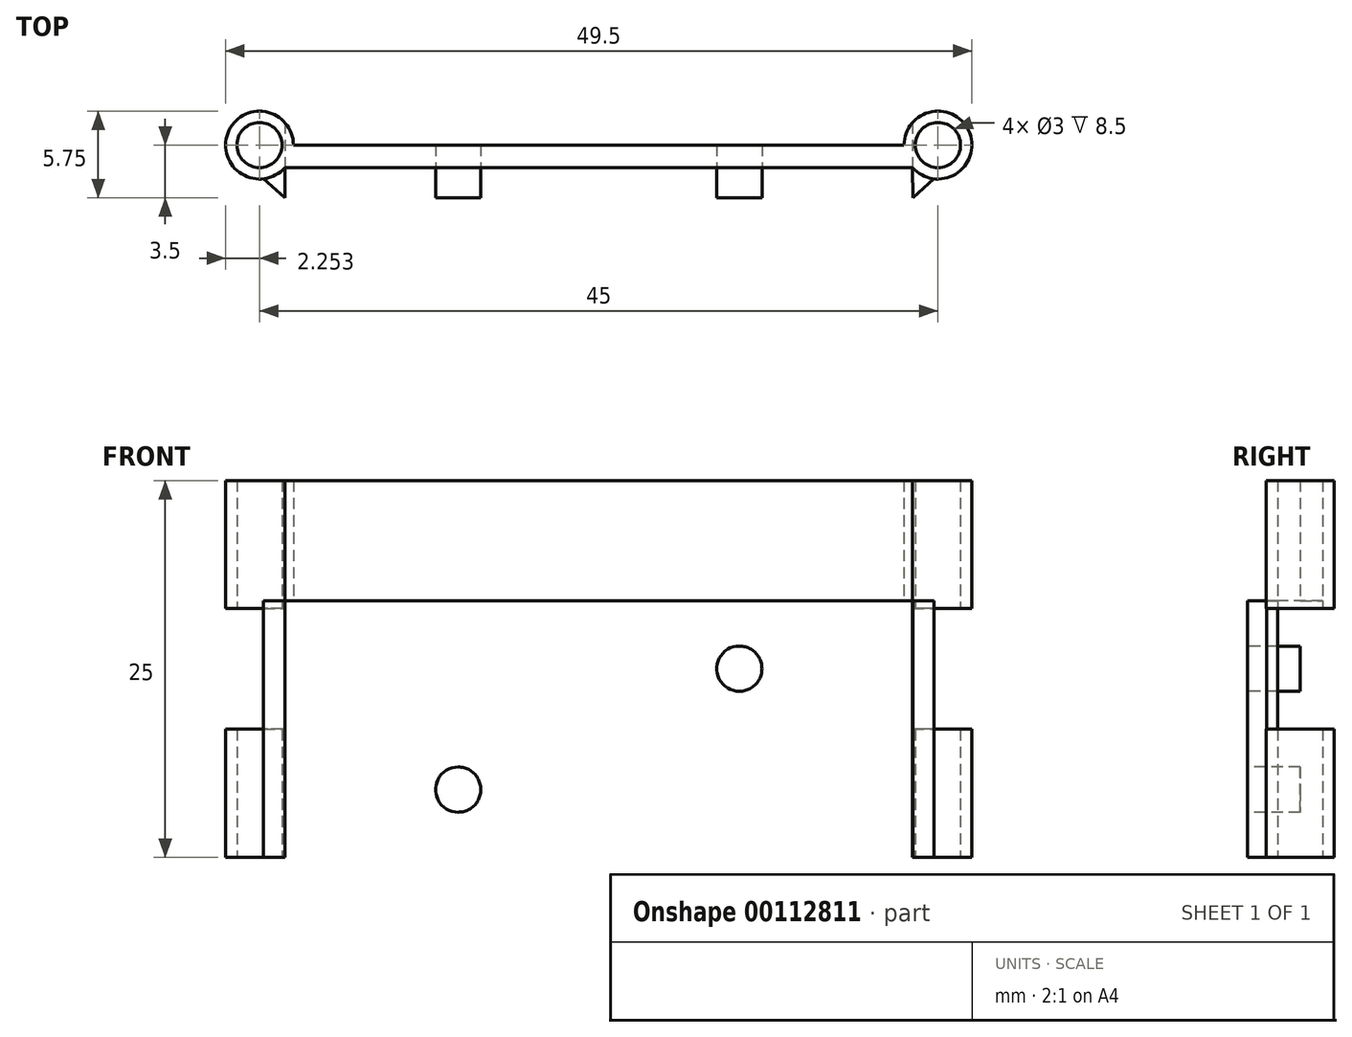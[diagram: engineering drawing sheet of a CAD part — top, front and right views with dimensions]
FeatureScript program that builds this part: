
annotation { "Feature Type Name" : "Feature", "Feature Type Description" : "" }
export const myFeature = defineFeature(function(context is Context, id is Id, definition is map)
    precondition{}
    {
        {
            var Q0;
            Q0=qCreatedBy(makeId("Top.planeOp"),FACE);
            var sketch = newSketch(context, id + "F0", { "sketchPlane" : qUnion([Q0])});
            skCircle(sketch, "E0", {"center": v(24.85, 0) * mm, "radius": 1.5 * mm});
            skCircle(sketch, "E1", {"center": v(-20.15, 0) * mm, "radius": 1.5 * mm});
            skLineSegment(sketch, "E2", {"start": v(-17.9, 0) * mm, "end": v(22.6, 0) * mm});
            skArc(sketch, "E3", {"start": v(-17.9, 0) * mm, "mid": v(-22.25, 0.8) * mm, "end": v(-18.47, -1.5) * mm});
            skArc(sketch, "E4", {"start": v(23.16, -1.49) * mm, "mid": v(26.96, 0.8) * mm, "end": v(22.6, 0) * mm});
            skPoint(sketch, "E5.orphan", {"position": v(-18.65, 0) * mm});
            skLineSegment(sketch, "E6.trimOffspring", {"start": v(23.16, -1.49) * mm, "end": v(-18.47, -1.5) * mm});
            skSolve(sketch);
        }
        {
            var Q0;
            Q0=makeQuery(id+"F0.imprint","IMPRINT",FACE,{"disambiguationData":[TD([[makeQuery(id+"F0.imprint","IMPRINT",EDGE,{"derivedFrom":sQuery(id+"F0.wireOp",EDGE,"E0")}),-1.0]])]});
            extrude(context, id + "F1", {"entities" : qUnion([Q0]), "depth" : 25 * mm});
        }
        {
            var Q0;
            Q0=makeQuery(id+"F1.opExtrude","CAP_FACE",FACE,{"disambiguationData":[OSD([sQuery(id+"F0.wireOp",EDGE,"E0"),sQuery(id+"F0.wireOp",EDGE,"E1"),sQuery(id+"F0.wireOp",EDGE,"E2"),sQuery(id+"F0.wireOp",EDGE,"E3"),sQuery(id+"F0.wireOp",EDGE,"E4"),sQuery(id+"F0.wireOp",EDGE,"E6.trimOffspring")])],"isStart":false});
            cPlane(context, id + "F2", {"entities" : qUnion([Q0]), "cplaneType" : CPlaneType.OFFSET, "offset" : 12.5 * mm, "oppositeDirection" : true, "width" : 152.4 * mm, "height" : 152.4 * mm});
        }
        {
            var Q0;
            Q0=qCreatedBy(id+"F2.planeOp",FACE);
            var sketch = newSketch(context, id + "F3", { "sketchPlane" : qUnion([Q0])});
            skCircle(sketch, "E7", {"center": v(-20.15, 0) * mm, "radius": 2.25 * mm});
            skCircle(sketch, "E8", {"center": v(24.85, 0) * mm, "radius": 2.25 * mm});
            skSolve(sketch);
        }
        {
            var Q0;
            Q0 = qSketchRegion(id + "F3", true);
            extrude(context, id + "F4", {"entities" : qUnion([Q0]), "operationType" : NewBodyOperationType.REMOVE, "oppositeDirection" : true, "depth" : 4 * mm, "hasSecondDirection" : true, "secondDirectionOppositeDirection" : false, "secondDirectionDepth" : 4 * mm});
        }
        {
            var Q0;
            Q0=makeQuery(id+"F1.opExtrude","CAP_FACE",FACE,{"disambiguationData":[OSD([sQuery(id+"F0.wireOp",EDGE,"E0"),sQuery(id+"F0.wireOp",EDGE,"E1"),sQuery(id+"F0.wireOp",EDGE,"E2"),sQuery(id+"F0.wireOp",EDGE,"E3"),sQuery(id+"F0.wireOp",EDGE,"E4"),sQuery(id+"F0.wireOp",EDGE,"E6.trimOffspring")])],"isStart":true});
            var sketch = newSketch(context, id + "F5", { "sketchPlane" : qUnion([Q0])});
            skLineSegment(sketch, "E9.0", {"start": v(23.18, 3.49) * mm, "end": v(-18.47, 3.5) * mm});
            skLineSegment(sketch, "E10", {"start": v(-18.47, 3.5) * mm, "end": v(-19.9, 2.24) * mm});
            skLineSegment(sketch, "E11", {"start": v(2.35, 1.5) * mm, "end": v(2.35, 0) * mm, "construction": true});
            skPoint(sketch, "E11.endSnap0", {"position": v(2.35, 0) * mm});
            skLineSegment(sketch, "E12.MirrorCS", {"start": v(23.18, 3.49) * mm, "end": v(24.6, 2.22) * mm});
            skSolve(sketch);
        }
        {
            var Q0;
            {var subQ3=sQuery(id+"F5.wireOp",EDGE,"E9.0");Q0=makeQuery(id+"F5.imprint","IMPRINT",FACE,{"disambiguationData":[TD([[makeQuery(id+"F5.imprint","IMPRINT",EDGE,{"derivedFrom":subQ3}),1.0]])]});}
            var Q1;
            Q1=makeQuery(id+"F4.boolean.opBoolean","COPY",FACE,{"derivedFrom":makeQuery(id+"F4.opExtrude","CAP_FACE",FACE,{"disambiguationData":[OSD([sQuery(id+"F3.wireOp",EDGE,"E8")])],"isStart":true})});
            extrude(context, id + "F6", {"entities" : qUnion([Q0]), "operationType" : NewBodyOperationType.ADD, "oppositeDirection" : true, "endBoundEntityFace" : qUnion([Q1]), "depth" : 17.02 * mm});
        }
        {
            var Q0;
            Q0=makeQuery(id+"F6.opExtrude","SWEPT_FACE",FACE,{"disambiguationData":[OSD([sQuery(id+"F5.wireOp",EDGE,"E9.0")])]});
            var sketch = newSketch(context, id + "F7", { "sketchPlane" : qUnion([Q0])});
            skCircle(sketch, "E13", {"center": v(-6.97, 12.52) * mm, "radius": 1.5 * mm});
            skLineSegment(sketch, "E14", {"start": v(-18.47, 8.5) * mm, "end": v(23.18, 8.5) * mm, "construction": true});
            skLineSegment(sketch, "E15", {"start": v(2.35, 17.02) * mm, "end": v(2.35, 0) * mm, "construction": true});
            skCircle(sketch, "E16.MirrorC", {"center": v(11.68, 12.52) * mm, "radius": 1.5 * mm});
            skCircle(sketch, "E17.MirrorC", {"center": v(-6.97, 4.5) * mm, "radius": 1.5 * mm});
            skCircle(sketch, "E18.MirrorC", {"center": v(11.68, 4.5) * mm, "radius": 1.5 * mm});
            skSolve(sketch);
        }
        {
            var Q0;
            Q0=makeQuery(id+"F7.imprint","IMPRINT",FACE,{"disambiguationData":[TD([[makeQuery(id+"F7.imprint","IMPRINT",EDGE,{"derivedFrom":sQuery(id+"F7.wireOp",EDGE,"E13")}),1.0]])]});
            var Q1;
            Q1=makeQuery(id+"F7.imprint","IMPRINT",FACE,{"disambiguationData":[TD([[makeQuery(id+"F7.imprint","IMPRINT",EDGE,{"derivedFrom":sQuery(id+"F7.wireOp",EDGE,"E17.MirrorC")}),-1.0]])]});
            var Q2;
            Q2=makeQuery(id+"F7.imprint","IMPRINT",FACE,{"disambiguationData":[TD([[makeQuery(id+"F7.imprint","IMPRINT",EDGE,{"derivedFrom":sQuery(id+"F7.wireOp",EDGE,"E18.MirrorC")}),1.0]])]});
            var Q3;
            Q3=makeQuery(id+"F7.imprint","IMPRINT",FACE,{"disambiguationData":[TD([[makeQuery(id+"F7.imprint","IMPRINT",EDGE,{"derivedFrom":sQuery(id+"F7.wireOp",EDGE,"E16.MirrorC")}),-1.0]])]});
            extrude(context, id + "F8", {"entities" : qUnion([Q0, Q1, Q2, Q3]), "operationType" : NewBodyOperationType.REMOVE, "oppositeDirection" : true, "depth" : 25.4 * mm});
        }
    });
